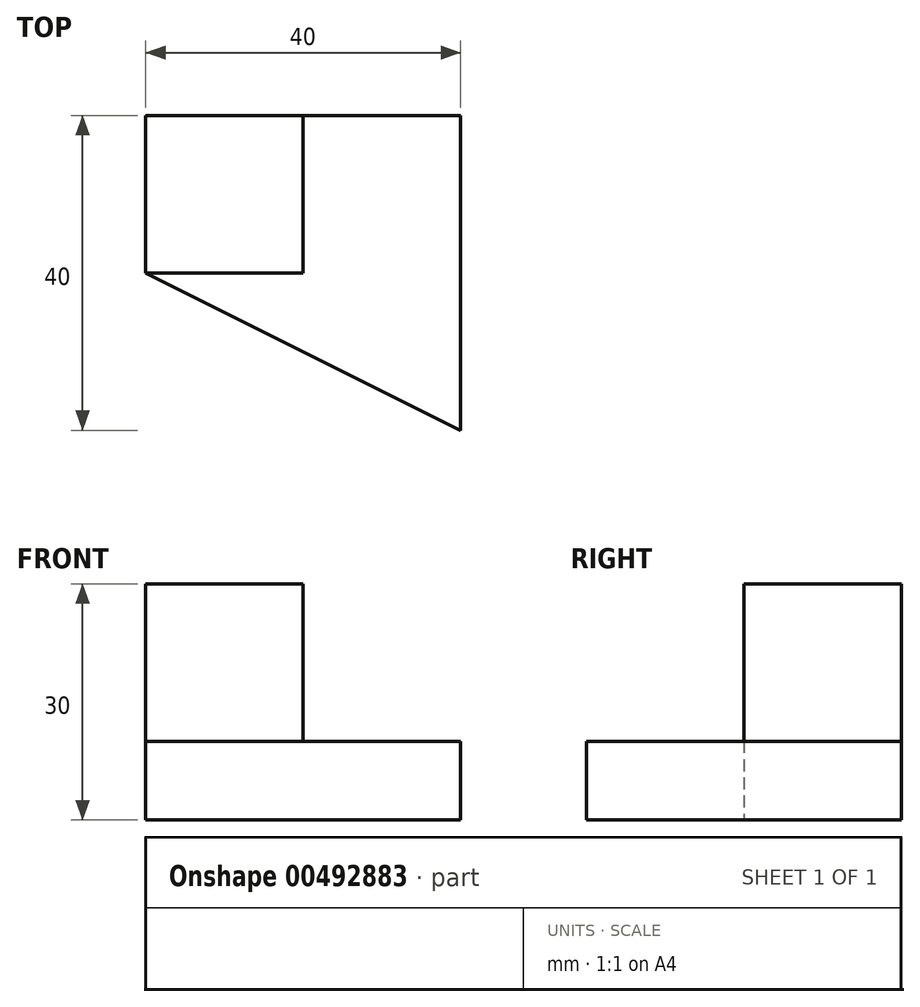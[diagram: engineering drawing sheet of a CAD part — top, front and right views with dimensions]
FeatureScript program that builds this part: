
annotation { "Feature Type Name" : "Feature", "Feature Type Description" : "" }
export const myFeature = defineFeature(function(context is Context, id is Id, definition is map)
    precondition{}
    {
        {
            var Q0;
            Q0=qCreatedBy(makeId("Top.planeOp"),FACE);
            var sketch = newSketch(context, id + "F0", { "sketchPlane" : qUnion([Q0])});
            skLineSegment(sketch, "E0", {"start": v(0, 0) * mm, "end": v(0, 20) * mm});
            skLineSegment(sketch, "E1", {"start": v(0, 20) * mm, "end": v(40, 20) * mm});
            skLineSegment(sketch, "E2", {"start": v(40, 20) * mm, "end": v(40, -20) * mm});
            skLineSegment(sketch, "E3", {"start": v(40, -20) * mm, "end": v(0, 0) * mm});
            skSolve(sketch);
        }
        {
            var Q0;
            Q0=makeQuery(id+"F0.imprint","IMPRINT",FACE,{"disambiguationData":[TD([[makeQuery(id+"F0.imprint","IMPRINT",EDGE,{"derivedFrom":sQuery(id+"F0.wireOp",EDGE,"E0")}),-1.0]])]});
            extrude(context, id + "F1", {"entities" : qUnion([Q0]), "depth" : 10 * mm});
        }
        {
            var Q0;
            Q0=makeQuery(id+"F1.opExtrude","CAP_FACE",FACE,{"disambiguationData":[OSD([sQuery(id+"F0.wireOp",EDGE,"E0"),sQuery(id+"F0.wireOp",EDGE,"E1"),sQuery(id+"F0.wireOp",EDGE,"E2"),sQuery(id+"F0.wireOp",EDGE,"E3")])],"isStart":false});
            var sketch = newSketch(context, id + "F2", { "sketchPlane" : qUnion([Q0])});
            skLineSegment(sketch, "E4", {"start": v(0, 20) * mm, "end": v(0, 0) * mm});
            skLineSegment(sketch, "E5", {"start": v(0, 0) * mm, "end": v(20, 0) * mm});
            skLineSegment(sketch, "E6", {"start": v(20, 0) * mm, "end": v(20, 20) * mm});
            skPoint(sketch, "E6.endSnap0", {"position": v(20, 20) * mm});
            skLineSegment(sketch, "E7", {"start": v(20, 20) * mm, "end": v(0, 20) * mm});
            skSolve(sketch);
        }
        {
            var Q0;
            Q0=qSketchRegion(id+"F2",true);
            extrude(context, id + "F3", {"entities" : qUnion([Q0]), "operationType" : NewBodyOperationType.ADD, "depth" : 20 * mm});
        }
    });
